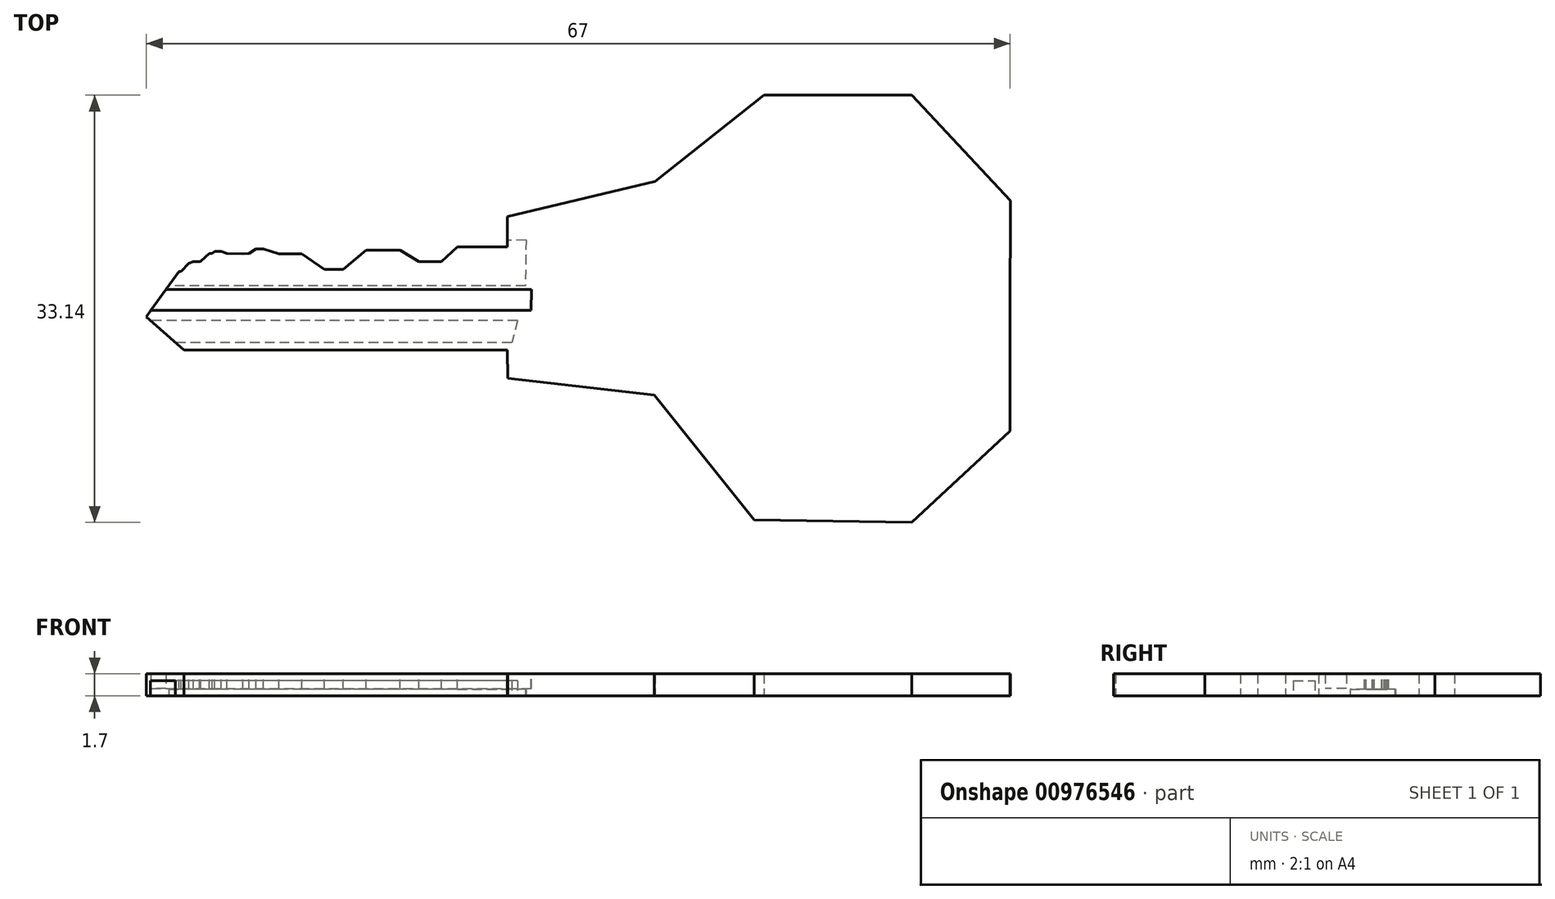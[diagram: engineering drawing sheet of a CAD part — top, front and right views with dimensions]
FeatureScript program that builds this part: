
annotation { "Feature Type Name" : "Feature", "Feature Type Description" : "" }
export const myFeature = defineFeature(function(context is Context, id is Id, definition is map)
    precondition{}
    {
        {
            var Q0;
            Q0=qCreatedBy(makeId("Top.planeOp"),FACE);
            var sketch = newSketch(context, id + "F0", { "sketchPlane" : qUnion([Q0])});
            skLineSegment(sketch, "E0", {"start": v(3.53, 5.42) * mm, "end": v(3.53, 7.78) * mm});
            skLineSegment(sketch, "E1.MirrorCS", {"start": v(-24.47, 0) * mm, "end": v(-21.54, -2.58) * mm});
            skLineSegment(sketch, "E2.MirrorCS", {"start": v(3.53, -2.58) * mm, "end": v(3.56, -4.75) * mm});
            skLineSegment(sketch, "E3.MirrorCS", {"start": v(3.53, 5.42) * mm, "end": v(-20.6, 5.42) * mm});
            skLineSegment(sketch, "E4.MirrorCS", {"start": v(-20.6, 5.42) * mm, "end": v(-24.47, 0) * mm});
            skLineSegment(sketch, "E5.MirrorCS", {"start": v(42.52, 0.11) * mm, "end": v(42.52, -8.85) * mm});
            skLineSegment(sketch, "E6.MirrorCS", {"start": v(-21.54, -2.58) * mm, "end": v(3.53, -2.58) * mm});
            skLineSegment(sketch, "E7.MirrorCS", {"start": v(34.9, -15.93) * mm, "end": v(22.68, -15.75) * mm});
            skLineSegment(sketch, "E8.MirrorCS", {"start": v(3.56, -4.75) * mm, "end": v(14.91, -6.07) * mm});
            skLineSegment(sketch, "E9.MirrorCS", {"start": v(22.68, -15.75) * mm, "end": v(14.91, -6.07) * mm});
            skLineSegment(sketch, "E10.MirrorCS", {"start": v(23.44, 17.21) * mm, "end": v(34.9, 17.21) * mm});
            skLineSegment(sketch, "E11.MirrorCS", {"start": v(42.52, -8.85) * mm, "end": v(34.9, -15.93) * mm});
            skLineSegment(sketch, "E12.MirrorCS", {"start": v(14.98, 10.53) * mm, "end": v(23.44, 17.21) * mm});
            skLineSegment(sketch, "E13.MirrorCS", {"start": v(3.53, 7.78) * mm, "end": v(14.98, 10.53) * mm});
            skLineSegment(sketch, "E14.MirrorCS", {"start": v(42.53, 9.01) * mm, "end": v(42.52, 0.11) * mm});
            skLineSegment(sketch, "E15.MirrorCS", {"start": v(34.9, 17.21) * mm, "end": v(42.53, 9.01) * mm});
            skSolve(sketch);
        }
        {
            var Q0;
            Q0 = qSketchRegion(id + "F0", true);
            extrude(context, id + "F1", {"entities" : qUnion([Q0]), "depth" : 1.7 * mm, "offsetDistance" : 25 * mm});
        }
        {
            var Q0;
            Q0=makeQuery(id+"F1.opExtrude","CAP_FACE",FACE,{"disambiguationData":[OSD([sQuery(id+"F0.wireOp",EDGE,"E0"),sQuery(id+"F0.wireOp",EDGE,"E1.MirrorCS"),sQuery(id+"F0.wireOp",EDGE,"E2.MirrorCS"),sQuery(id+"F0.wireOp",EDGE,"E3.MirrorCS"),sQuery(id+"F0.wireOp",EDGE,"E4.MirrorCS"),sQuery(id+"F0.wireOp",EDGE,"E5.MirrorCS"),sQuery(id+"F0.wireOp",EDGE,"E6.MirrorCS"),sQuery(id+"F0.wireOp",EDGE,"E7.MirrorCS"),sQuery(id+"F0.wireOp",EDGE,"E8.MirrorCS"),sQuery(id+"F0.wireOp",EDGE,"E9.MirrorCS"),sQuery(id+"F0.wireOp",EDGE,"E10.MirrorCS"),sQuery(id+"F0.wireOp",EDGE,"E11.MirrorCS"),sQuery(id+"F0.wireOp",EDGE,"E12.MirrorCS"),sQuery(id+"F0.wireOp",EDGE,"E13.MirrorCS"),sQuery(id+"F0.wireOp",EDGE,"E14.MirrorCS"),sQuery(id+"F0.wireOp",EDGE,"E15.MirrorCS")])],"isStart":true});
            var sketch = newSketch(context, id + "F2", { "sketchPlane" : qUnion([Q0])});
            skLineSegment(sketch, "E16", {"start": v(4.31, 0.28) * mm, "end": v(-26.62, 0.28) * mm});
            skLineSegment(sketch, "E17", {"start": v(3.87, 1.98) * mm, "end": v(-25.99, 1.98) * mm});
            skLineSegment(sketch, "E18", {"start": v(4.31, 0.28) * mm, "end": v(3.87, 1.98) * mm});
            skLineSegment(sketch, "E19", {"start": v(-25.99, 1.98) * mm, "end": v(-26.62, 0.28) * mm});
            skSolve(sketch);
        }
        {
            var Q0;
            {var subQ0=sQuery(id+"F2.wireOp",EDGE,"E18");Q0=makeQuery(id+"F2.imprint","IMPRINT",FACE,{"disambiguationData":[TD([[makeQuery(id+"F2.imprint","IMPRINT",EDGE,{"derivedFrom":subQ0}),1.0]])]});}
            var Q1;
            {var subQ0=sQuery(id+"F2.wireOp",EDGE,"E19");Q1=makeQuery(id+"F2.imprint","IMPRINT",FACE,{"disambiguationData":[TD([[makeQuery(id+"F2.imprint","IMPRINT",EDGE,{"derivedFrom":subQ0}),1.0]])]});}
            extrude(context, id + "F3", {"entities" : qUnion([Q0, Q1]), "operationType" : NewBodyOperationType.REMOVE, "oppositeDirection" : true, "depth" : 1.15 * mm, "offsetDistance" : 25 * mm});
        }
        {
            var Q0;
            Q0=makeQuery(id+"F1.opExtrude","CAP_FACE",FACE,{"disambiguationData":[OSD([sQuery(id+"F0.wireOp",EDGE,"E0"),sQuery(id+"F0.wireOp",EDGE,"E1.MirrorCS"),sQuery(id+"F0.wireOp",EDGE,"E2.MirrorCS"),sQuery(id+"F0.wireOp",EDGE,"E3.MirrorCS"),sQuery(id+"F0.wireOp",EDGE,"E4.MirrorCS"),sQuery(id+"F0.wireOp",EDGE,"E5.MirrorCS"),sQuery(id+"F0.wireOp",EDGE,"E6.MirrorCS"),sQuery(id+"F0.wireOp",EDGE,"E7.MirrorCS"),sQuery(id+"F0.wireOp",EDGE,"E8.MirrorCS"),sQuery(id+"F0.wireOp",EDGE,"E9.MirrorCS"),sQuery(id+"F0.wireOp",EDGE,"E10.MirrorCS"),sQuery(id+"F0.wireOp",EDGE,"E11.MirrorCS"),sQuery(id+"F0.wireOp",EDGE,"E12.MirrorCS"),sQuery(id+"F0.wireOp",EDGE,"E13.MirrorCS"),sQuery(id+"F0.wireOp",EDGE,"E14.MirrorCS"),sQuery(id+"F0.wireOp",EDGE,"E15.MirrorCS")])],"isStart":false});
            var sketch = newSketch(context, id + "F4", { "sketchPlane" : qUnion([Q0])});
            skLineSegment(sketch, "E20", {"start": v(-25.62, 2.14) * mm, "end": v(5.4, 2.14) * mm});
            skLineSegment(sketch, "E21", {"start": v(-26.04, 0.5) * mm, "end": v(5.37, 0.5) * mm});
            skLineSegment(sketch, "E22", {"start": v(-25.62, 2.14) * mm, "end": v(-26.04, 0.5) * mm});
            skLineSegment(sketch, "E23", {"start": v(5.4, 2.14) * mm, "end": v(5.37, 0.5) * mm});
            skSolve(sketch);
        }
        {
            var Q0;
            Q0 = qSketchRegion(id + "F4", true);
            extrude(context, id + "F5", {"entities" : qUnion([Q0]), "operationType" : NewBodyOperationType.REMOVE, "oppositeDirection" : true, "depth" : 1.15 * mm, "offsetDistance" : 25 * mm});
        }
        {
            var Q0;
            Q0=makeQuery(id+"F1.opExtrude","CAP_FACE",FACE,{"disambiguationData":[OSD([sQuery(id+"F0.wireOp",EDGE,"E0"),sQuery(id+"F0.wireOp",EDGE,"E1.MirrorCS"),sQuery(id+"F0.wireOp",EDGE,"E2.MirrorCS"),sQuery(id+"F0.wireOp",EDGE,"E3.MirrorCS"),sQuery(id+"F0.wireOp",EDGE,"E4.MirrorCS"),sQuery(id+"F0.wireOp",EDGE,"E5.MirrorCS"),sQuery(id+"F0.wireOp",EDGE,"E6.MirrorCS"),sQuery(id+"F0.wireOp",EDGE,"E7.MirrorCS"),sQuery(id+"F0.wireOp",EDGE,"E8.MirrorCS"),sQuery(id+"F0.wireOp",EDGE,"E9.MirrorCS"),sQuery(id+"F0.wireOp",EDGE,"E10.MirrorCS"),sQuery(id+"F0.wireOp",EDGE,"E11.MirrorCS"),sQuery(id+"F0.wireOp",EDGE,"E12.MirrorCS"),sQuery(id+"F0.wireOp",EDGE,"E13.MirrorCS"),sQuery(id+"F0.wireOp",EDGE,"E14.MirrorCS"),sQuery(id+"F0.wireOp",EDGE,"E15.MirrorCS")])],"isStart":false});
            var sketch = newSketch(context, id + "F6", { "sketchPlane" : qUnion([Q0])});
            skLineSegment(sketch, "E24", {"start": v(-0.33, 5.42) * mm, "end": v(-1.58, 4.28) * mm});
            skLineSegment(sketch, "E25", {"start": v(-1.58, 4.28) * mm, "end": v(-3.34, 4.28) * mm});
            skLineSegment(sketch, "E26", {"start": v(-3.34, 4.28) * mm, "end": v(-4.8, 5.2) * mm});
            skLineSegment(sketch, "E27", {"start": v(-4.8, 5.2) * mm, "end": v(-7.41, 5.2) * mm});
            skLineSegment(sketch, "E28", {"start": v(-7.41, 5.2) * mm, "end": v(-9.2, 3.69) * mm});
            skLineSegment(sketch, "E29", {"start": v(-9.2, 3.69) * mm, "end": v(-10.66, 3.69) * mm});
            skLineSegment(sketch, "E30", {"start": v(-10.66, 3.69) * mm, "end": v(-12.4, 4.89) * mm});
            skLineSegment(sketch, "E31", {"start": v(-12.4, 4.89) * mm, "end": v(-14.19, 4.89) * mm});
            skLineSegment(sketch, "E32", {"start": v(-14.19, 4.89) * mm, "end": v(-15.38, 5.3) * mm});
            skLineSegment(sketch, "E33", {"start": v(-15.38, 5.3) * mm, "end": v(-15.98, 5.3) * mm});
            skLineSegment(sketch, "E34", {"start": v(-15.98, 5.3) * mm, "end": v(-16.52, 4.92) * mm});
            skLineSegment(sketch, "E35", {"start": v(-16.52, 4.92) * mm, "end": v(-17, 4.89) * mm});
            skLineSegment(sketch, "E36", {"start": v(-17, 4.89) * mm, "end": v(-18.23, 4.92) * mm});
            skLineSegment(sketch, "E37", {"start": v(-18.23, 4.92) * mm, "end": v(-18.66, 5.07) * mm});
            skLineSegment(sketch, "E38", {"start": v(-18.66, 5.07) * mm, "end": v(-19.18, 5.07) * mm});
            skLineSegment(sketch, "E39", {"start": v(-19.18, 5.07) * mm, "end": v(-19.36, 4.92) * mm});
            skLineSegment(sketch, "E40", {"start": v(-19.36, 4.92) * mm, "end": v(-19.6, 4.92) * mm});
            skLineSegment(sketch, "E41", {"start": v(-19.6, 4.92) * mm, "end": v(-20.24, 4.32) * mm});
            skLineSegment(sketch, "E42", {"start": v(-20.24, 4.32) * mm, "end": v(-20.35, 4.28) * mm});
            skLineSegment(sketch, "E43", {"start": v(-20.35, 4.28) * mm, "end": v(-20.83, 4.28) * mm});
            skLineSegment(sketch, "E44", {"start": v(-20.83, 4.28) * mm, "end": v(-21.17, 4.16) * mm});
            skLineSegment(sketch, "E45", {"start": v(-21.17, 4.16) * mm, "end": v(-21.8, 3.53) * mm});
            skLineSegment(sketch, "E46", {"start": v(-21.8, 3.53) * mm, "end": v(-21.95, 3.53) * mm});
            skLineSegment(sketch, "E47", {"start": v(-21.95, 3.53) * mm, "end": v(-23.24, 4.84) * mm});
            skLineSegment(sketch, "E48", {"start": v(-23.24, 4.84) * mm, "end": v(-22.14, 7.95) * mm});
            skLineSegment(sketch, "E49", {"start": v(-22.14, 7.95) * mm, "end": v(0, 7.78) * mm});
            skLineSegment(sketch, "E50", {"start": v(0, 7.78) * mm, "end": v(-0.33, 5.42) * mm});
            skLineSegment(sketch, "E51", {"start": v(-21.95, 3.53) * mm, "end": v(-20.9, 6) * mm});
            skLineSegment(sketch, "E52", {"start": v(-0.33, 5.42) * mm, "end": v(-5.38, 6.79) * mm});
            skLineSegment(sketch, "E53", {"start": v(-20.9, 6) * mm, "end": v(-5.38, 6.79) * mm});
            skSolve(sketch);
        }
        {
            var Q0;
            {var subQ6=sQuery(id+"F6.wireOp",EDGE,"E47");Q0=makeQuery(id+"F6.imprint","IMPRINT",FACE,{"disambiguationData":[TD([[makeQuery(id+"F6.imprint","IMPRINT",EDGE,{"derivedFrom":subQ6}),-1.0]])]});}
            var Q1;
            {var subQ5=sQuery(id+"F6.wireOp",EDGE,"E24");Q1=makeQuery(id+"F6.imprint","IMPRINT",FACE,{"disambiguationData":[TD([[makeQuery(id+"F6.imprint","IMPRINT",EDGE,{"derivedFrom":subQ5}),-1.0]])]});}
            extrude(context, id + "F7", {"entities" : qUnion([Q0, Q1]), "operationType" : NewBodyOperationType.REMOVE, "oppositeDirection" : true, "depth" : 25 * mm, "offsetDistance" : 25 * mm});
        }
        {
            var Q0;
            Q0=makeQuery(id+"F1.opExtrude","CAP_FACE",FACE,{"disambiguationData":[OSD([sQuery(id+"F0.wireOp",EDGE,"E0"),sQuery(id+"F0.wireOp",EDGE,"E1.MirrorCS"),sQuery(id+"F0.wireOp",EDGE,"E2.MirrorCS"),sQuery(id+"F0.wireOp",EDGE,"E3.MirrorCS"),sQuery(id+"F0.wireOp",EDGE,"E4.MirrorCS"),sQuery(id+"F0.wireOp",EDGE,"E5.MirrorCS"),sQuery(id+"F0.wireOp",EDGE,"E6.MirrorCS"),sQuery(id+"F0.wireOp",EDGE,"E7.MirrorCS"),sQuery(id+"F0.wireOp",EDGE,"E8.MirrorCS"),sQuery(id+"F0.wireOp",EDGE,"E9.MirrorCS"),sQuery(id+"F0.wireOp",EDGE,"E10.MirrorCS"),sQuery(id+"F0.wireOp",EDGE,"E11.MirrorCS"),sQuery(id+"F0.wireOp",EDGE,"E12.MirrorCS"),sQuery(id+"F0.wireOp",EDGE,"E13.MirrorCS"),sQuery(id+"F0.wireOp",EDGE,"E14.MirrorCS"),sQuery(id+"F0.wireOp",EDGE,"E15.MirrorCS")])],"isStart":true});
            var sketch = newSketch(context, id + "F8", { "sketchPlane" : qUnion([Q0])});
            skLineSegment(sketch, "E54", {"start": v(4.93, -2.42) * mm, "end": v(-25.24, -2.42) * mm});
            skLineSegment(sketch, "E55", {"start": v(4.98, -5.97) * mm, "end": v(-25.59, -5.42) * mm});
            skLineSegment(sketch, "E56", {"start": v(-25.59, -5.42) * mm, "end": v(-25.24, -2.42) * mm});
            skLineSegment(sketch, "E57", {"start": v(4.98, -5.97) * mm, "end": v(4.93, -2.42) * mm});
            skLineSegment(sketch, "E58", {"start": v(3.53, 2.58) * mm, "end": v(-21.54, 2.58) * mm});
            skSolve(sketch);
        }
        {
            var Q0;
            Q0 = qSketchRegion(id + "F8", true);
            extrude(context, id + "F9", {"entities" : qUnion([Q0]), "operationType" : NewBodyOperationType.REMOVE, "oppositeDirection" : true, "depth" : 0.5 * mm, "offsetDistance" : 25 * mm});
        }
    });
